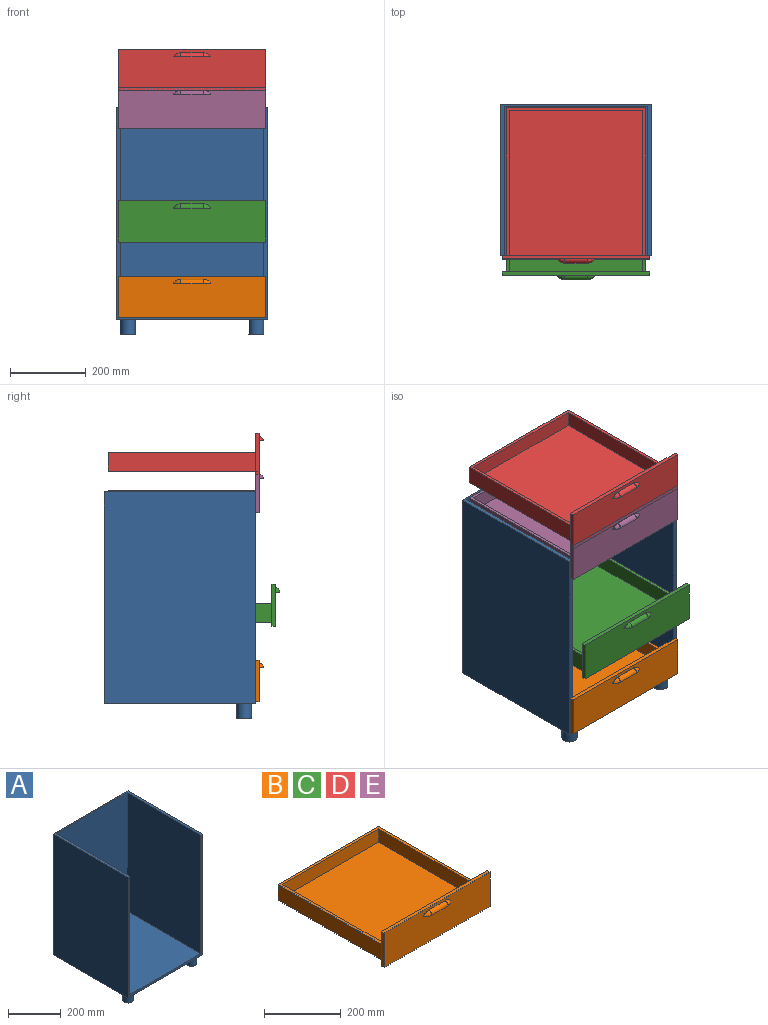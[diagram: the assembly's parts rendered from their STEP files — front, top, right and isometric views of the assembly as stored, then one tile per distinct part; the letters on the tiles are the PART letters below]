
ASSEMBLY  parts=5 mates=4
PART A: 14 faces, bbox 400x400x600 mm
  f0: plane 560x400mm, normal (0,1,0), area 224000mm2, adj f1,f3,f4,f5
  f1: plane 560x400mm, normal (-1,0,0), area 224000mm2, adj f0,f2,f4,f5
  f2: plane 560x400mm, normal (0,-1,0), area 15000mm2, adj f1,f3,f4,f5,f7,f8,f9
  f3: plane 560x400mm, normal (1,0,0), area 224000mm2, adj f0,f2,f4,f5
  f4: plane 400x400mm, normal (0,0,1), area 9900mm2, adj f0,f1,f2,f3,f6,f7,f8
  f5: plane 400x400mm, normal (0,0,-1), area 157486.7mm2, adj f0,f1,f2,f3,f10,f13
  f6: plane 550x380mm, normal (0,-1,0), area 209000mm2, adj f4,f7,f8,f9
  f7: plane 550x395mm, normal (1,0,0), area 217250mm2, adj f2,f4,f6,f9
  f8: plane 550x395mm, normal (-1,0,0), area 217250mm2, adj f2,f4,f6,f9
  f9: plane 395x380mm, normal (0,0,1), area 150100mm2, adj f2,f6,f7,f8
  f10: cylinder r=20mm len=40mm, axis (0,0,-1), area 5026.5mm2, adj f5,f11
  f11: plane 40x40mm, normal (0,0,-1), area 1256.6mm2, adj f10
  f12: plane 40x40mm, normal (0,0,-1), area 1256.6mm2, adj f13
  f13: cylinder r=20mm len=40mm, axis (0,0,-1), area 5026.5mm2, adj f5,f12
PART B: 24 faces, bbox 390x411x110 mm
  f0: plane 390x110mm, normal (0,-1,0), area 42592mm2, adj f7,f8,f9,f10,f17,f18,f19,f20
  f1: plane 390x50mm, normal (-1,0,0), area 19500mm2, adj f3,f4,f5,f6
  f2: plane 390x50mm, normal (1,0,0), area 19500mm2, adj f3,f4,f5,f6
  f3: plane 370x50mm, normal (0,1,0), area 18500mm2, adj f1,f2,f4,f5
  f4: plane 390x370mm, normal (0,0,1), area 9072mm2, adj f1,f2,f3,f6,f12,f13,f14
  f5: plane 390x370mm, normal (0,0,-1), area 144300mm2, adj f1,f2,f3,f6
  f6: plane 390x110mm, normal (0,1,0), area 24400mm2, adj f1,f2,f4,f5,f7,f8,f9,f10
  f7: plane 110x10mm, normal (-1,0,0), area 1100mm2, adj f0,f6,f9,f10
  f8: plane 110x10mm, normal (1,0,0), area 1100mm2, adj f0,f6,f9,f10
  f9: plane 390x10mm, normal (0,0,1), area 3900mm2, adj f0,f6,f7,f8
  f10: plane 390x10mm, normal (0,0,-1), area 3900mm2, adj f0,f6,f7,f8
  f11: plane 354x42mm, normal (0,1,0), area 14868mm2, adj f12,f13,f15,f16
  f12: plane 384x42mm, normal (1,0,0), area 16128mm2, adj f4,f11,f14,f15,f16
  f13: plane 384x42mm, normal (-1,0,0), area 16128mm2, adj f4,f11,f14,f15,f16
  f14: plane 354x42mm, normal (0,-1,0), area 14868mm2, adj f4,f12,f13,f16
  f15: plane 354x2mm, normal (0,0,-1), area 708mm2, adj f6,f11,f12,f13
  f16: plane 384x354mm, normal (0,0,1), area 135936mm2, adj f11,f12,f13,f14
  f17: revolved ~16.34x8mm, area 155.5mm2, adj f0,f18,f23
  f18: cylinder r=8mm len=60mm, axis (1,0,0), area 754mm2, adj f0,f17,f19,f23
  f19: revolved ~16.34x8mm, area 155.5mm2, adj f0,f18,f23
  f20: revolved ~20x11mm, area 269.5mm2, adj f0,f21,f23
  f21: cylinder r=11mm len=60mm, axis (1,0,0), area 1036.7mm2, adj f0,f20,f22,f23
  f22: revolved ~20x11mm, area 269.5mm2, adj f0,f21,f23
  f23: plane 100x11mm, normal (0,0,-1), area 308mm2, adj f0,f17,f18,f19,f20,f21,f22
PART C: same geometry as B
PART D: same geometry as B
PART E: same geometry as B
PLACE A at identity fixed
PLACE B at identity
PLACE C t=(0,-43.5,200)mm
PLACE D t=(0,0,600)mm
PLACE E t=(0,0,500)mm
MATE slider D.f6 <-> A.f2  axis (0,-1,0) through (0,-400,650)mm
MATE slider B.f6 <-> A.f2  axis (0,-1,0) through (0,-400,50)mm
MATE slider C.f6 <-> A.f2  axis (0,-1,0) through (0,-443.5,250)mm
MATE slider E.f6 <-> A.f2  axis (0,-1,0) through (0,-400,550)mm
